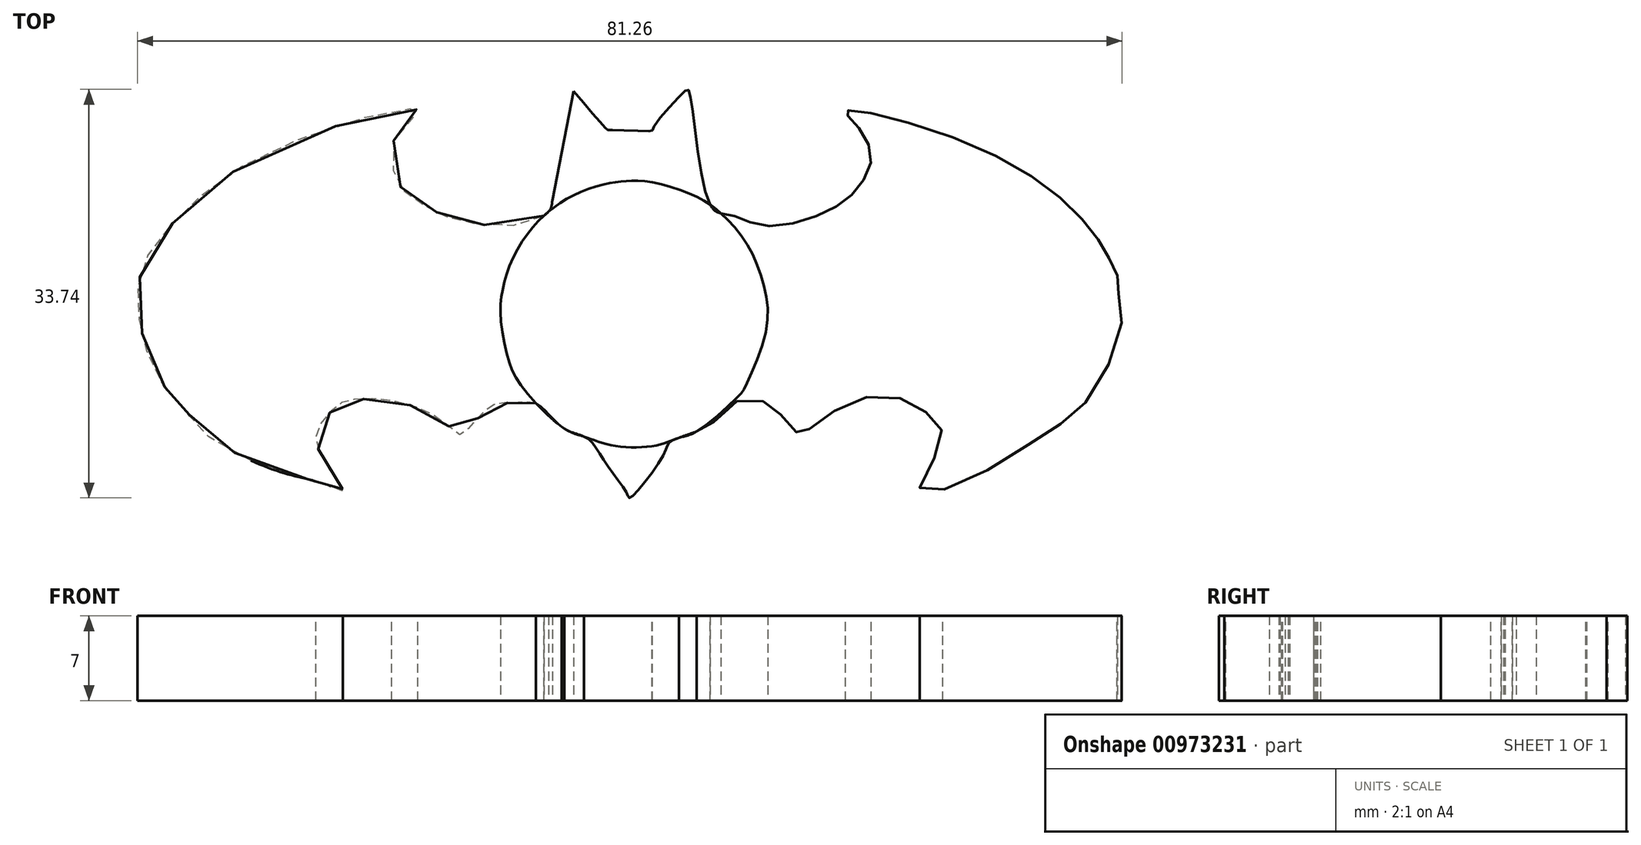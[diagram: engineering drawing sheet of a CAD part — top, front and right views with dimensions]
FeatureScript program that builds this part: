
annotation { "Feature Type Name" : "Feature", "Feature Type Description" : "" }
export const myFeature = defineFeature(function(context is Context, id is Id, definition is map)
    precondition{}
    {
        {
            var Q0;
            Q0=qCreatedBy(makeId("Top.planeOp"),FACE);
            var sketch = newSketch(context, id + "F0", { "sketchPlane" : qUnion([Q0])});
            skFitSpline(sketch, "E0", {"points": [v(-4.97, 18.4) * mm, v(-2.22, 15.26) * mm, v(-2.02, 15.22) * mm, v(1.53, 15.14) * mm, v(1.53, 15.22) * mm, v(4.16, 18.37) * mm, v(4.56, 18.45) * mm, v(6.34, 8.99) * mm, v(7.99, 8.2) * mm, v(10.58, 7.33) * mm, v(15.52, 8.29) * mm, v(18.5, 10.4) * mm, v(19.58, 13.3) * mm, v(17.99, 16.06) * mm, v(17.51, 16.78) * mm, v(28.87, 13.55) * mm, v(37.9, 6.79) * mm, v(39.94, 3.16) * mm], "startDerivative": vector(56.58, -66.21) * mm, "endDerivative": vector(23.78, -52.66) * mm});
            skFitSpline(sketch, "E1", {"points": [v(39.94, 3.16) * mm, v(39.94, 2.1) * mm, v(40.27, -0.8) * mm, v(37.31, -7.26) * mm, v(34.01, -9.85) * mm, v(27.07, -13.94) * mm, v(23.62, -14.4) * mm, v(25.45, -10.55) * mm, v(24.94, -8.9) * mm, v(22.76, -7.23) * mm, v(18.8, -6.97) * mm, v(15.07, -9.06) * mm, v(13.72, -9.9) * mm, v(13.34, -9.66) * mm, v(11.82, -7.96) * mm, v(10.39, -7.15) * mm, v(8.28, -7.24) * mm, v(8.2, -7.33) * mm, v(7.45, -8.22) * mm, v(6.45, -9.02) * mm, v(5.19, -9.7) * mm, v(2.95, -10.6) * mm, v(2.55, -11.48) * mm, v(-0.32, -15.17) * mm, v(-0.52, -14.9) * mm, v(-2.3, -12.33) * mm, v(-3.7, -10.36) * mm, v(-4.97, -9.81) * mm, v(-6.29, -9.03) * mm, v(-8.25, -7.28) * mm, v(-9.37, -7.31) * mm, v(-10.15, -7.31) * mm, v(-11.2, -7.4) * mm, v(-11.98, -7.71) * mm, v(-14.2, -9.96) * mm, v(-14.44, -9.9) * mm, v(-16.48, -8.38) * mm, v(-18.28, -7.59) * mm, v(-20.56, -7.06) * mm, v(-23.45, -7.11) * mm, v(-24.54, -7.6) * mm, v(-26.03, -9.39) * mm, v(-26.08, -11.07) * mm, v(-24.47, -13.8) * mm, v(-24.04, -14.6) * mm, v(-25.18, -14.15) * mm, v(-30.01, -12.75) * mm, v(-36.3, -9.08) * mm, v(-36.84, -7.97) * mm, v(-37.85, -7.07) * mm, v(-39.83, -3.97) * mm, v(-40.86, 0) * mm, v(-40.57, 3.8) * mm, v(-37.46, 8.14) * mm, v(-29.77, 13.55) * mm, v(-18.12, 16.95) * mm, v(-17.85, 16.66) * mm, v(-19.52, 14.96) * mm, v(-19.8, 11.64) * mm, v(-18.75, 10) * mm, v(-16.57, 8.59) * mm, v(-14.93, 7.88) * mm, v(-10.07, 7.33) * mm, v(-7.02, 8.47) * mm, v(-6.72, 9.4) * mm], "startDerivative": vector(-9.1, -93.87) * mm, "endDerivative": vector(8.09, 94.73) * mm});
            skFitSpline(sketch, "E2", {"points": [v(-6.72, 9.4) * mm, v(-4.97, 18.4) * mm], "startDerivative": vector(1.75, 9.02) * mm, "endDerivative": vector(1.75, 9.02) * mm});
            skFitSpline(sketch, "E3", {"points": [v(7.24, 8.29) * mm, v(9.3, 5.88) * mm, v(10.72, 2.48) * mm, v(10.9, -1.49) * mm, v(9.2, -6.04) * mm, v(8.72, -6.71) * mm, v(5.19, -9.7) * mm, v(3.73, -10.22) * mm, v(2.16, -10.79) * mm, v(-1.65, -10.87) * mm, v(-4.1, -10.12) * mm, v(-5.72, -9.47) * mm, v(-9.2, -6.02) * mm, v(-10.36, -3.69) * mm, v(-11, 0) * mm, v(-10.8, 2.05) * mm, v(-10.12, 4.32) * mm, v(-8.64, 6.81) * mm, v(-7.02, 8.47) * mm, v(-4.78, 9.9) * mm, v(-2.14, 10.8) * mm, v(-0.65, 10.98) * mm, v(1.26, 10.93) * mm, v(5.19, 9.7) * mm, v(7.24, 8.29) * mm]});
            skSolve(sketch);
        }
        {
            var Q0;
            {var subQ0=sQuery(id+"F0.wireOp",EDGE,"E2");Q0=makeQuery(id+"F0.imprint","IMPRINT",FACE,{"disambiguationData":[TD([[makeQuery(id+"F0.imprint","IMPRINT",EDGE,{"derivedFrom":subQ0}),-1.0]])]});}
            var Q1;
            {var subQ0=sQuery(id+"F0.wireOp",EDGE,"E3");var subQ1=sQuery(id+"F0.wireOp",EDGE,"E0");var subQ2=makeQuery(id+"F0.imprint","INTERSECT",VERTEX,{"disambiguationData":[OD(0.0)],"derivedFrom":[subQ1,subQ0]});Q1=makeQuery(id+"F0.imprint","IMPRINT",FACE,{"disambiguationData":[TD([[makeQuery(id+"F0.imprint","IMPRINT",EDGE,{"disambiguationData":[TD([[subQ2,-1.0]])],"derivedFrom":subQ1}),1.0]])]});}
            var Q2;
            {var subQ0=sQuery(id+"F0.wireOp",EDGE,"E1");var subQ1=sQuery(id+"F0.wireOp",EDGE,"E0");var subQ2=makeQuery(id+"F0.imprint","INTERSECT",VERTEX,{"derivedFrom":[subQ1,subQ0]});Q2=makeQuery(id+"F0.imprint","IMPRINT",FACE,{"disambiguationData":[TD([[makeQuery(id+"F0.imprint","IMPRINT",EDGE,{"disambiguationData":[TD([[subQ2,1.0]])],"derivedFrom":subQ1}),-1.0]])]});}
            var Q3;
            {var subQ0=sQuery(id+"F0.wireOp",EDGE,"E3");var subQ1=sQuery(id+"F0.wireOp",EDGE,"E1");var subQ2=makeQuery(id+"F0.imprint","INTERSECT",VERTEX,{"disambiguationData":[OD(0.0)],"derivedFrom":[subQ1,subQ0]});Q3=makeQuery(id+"F0.imprint","IMPRINT",FACE,{"disambiguationData":[TD([[makeQuery(id+"F0.imprint","IMPRINT",EDGE,{"disambiguationData":[TD([[subQ2,-1.0]])],"derivedFrom":subQ1}),1.0]])]});}
            var Q4;
            {var subQ0=sQuery(id+"F0.wireOp",EDGE,"E3");var subQ1=sQuery(id+"F0.wireOp",EDGE,"E1");var subQ2=makeQuery(id+"F0.imprint","INTERSECT",VERTEX,{"disambiguationData":[OD(1.0)],"derivedFrom":[subQ1,subQ0]});Q4=makeQuery(id+"F0.imprint","IMPRINT",FACE,{"disambiguationData":[TD([[makeQuery(id+"F0.imprint","IMPRINT",EDGE,{"disambiguationData":[TD([[subQ2,-1.0]])],"derivedFrom":subQ1}),-1.0]])]});}
            var Q5;
            {var subQ0=sQuery(id+"F0.wireOp",EDGE,"E3");var subQ1=sQuery(id+"F0.wireOp",EDGE,"E1");var subQ2=makeQuery(id+"F0.imprint","INTERSECT",VERTEX,{"disambiguationData":[OD(2.0)],"derivedFrom":[subQ1,subQ0]});Q5=makeQuery(id+"F0.imprint","IMPRINT",FACE,{"disambiguationData":[TD([[makeQuery(id+"F0.imprint","IMPRINT",EDGE,{"disambiguationData":[TD([[subQ2,-1.0]])],"derivedFrom":subQ1}),1.0]])]});}
            var Q6;
            {var subQ0=sQuery(id+"F0.wireOp",EDGE,"E3");var subQ1=sQuery(id+"F0.wireOp",EDGE,"E1");var subQ2=makeQuery(id+"F0.imprint","INTERSECT",VERTEX,{"disambiguationData":[OD(3.0)],"derivedFrom":[subQ1,subQ0]});Q6=makeQuery(id+"F0.imprint","IMPRINT",FACE,{"disambiguationData":[TD([[makeQuery(id+"F0.imprint","IMPRINT",EDGE,{"disambiguationData":[TD([[subQ2,-1.0]])],"derivedFrom":subQ1}),-1.0]])]});}
            var Q7;
            {var subQ0=sQuery(id+"F0.wireOp",EDGE,"E3");var subQ1=sQuery(id+"F0.wireOp",EDGE,"E1");var subQ2=makeQuery(id+"F0.imprint","INTERSECT",VERTEX,{"disambiguationData":[OD(4.0)],"derivedFrom":[subQ1,subQ0]});Q7=makeQuery(id+"F0.imprint","IMPRINT",FACE,{"disambiguationData":[TD([[makeQuery(id+"F0.imprint","IMPRINT",EDGE,{"disambiguationData":[TD([[subQ2,-1.0]])],"derivedFrom":subQ1}),1.0]])]});}
            var Q8;
            {var subQ0=sQuery(id+"F0.wireOp",EDGE,"E3");var subQ1=sQuery(id+"F0.wireOp",EDGE,"E1");var subQ2=makeQuery(id+"F0.imprint","INTERSECT",VERTEX,{"disambiguationData":[OD(5.0)],"derivedFrom":[subQ1,subQ0]});Q8=makeQuery(id+"F0.imprint","IMPRINT",FACE,{"disambiguationData":[TD([[makeQuery(id+"F0.imprint","IMPRINT",EDGE,{"disambiguationData":[TD([[subQ2,-1.0]])],"derivedFrom":subQ1}),-1.0]])]});}
            var Q9;
            {var subQ0=sQuery(id+"F0.wireOp",EDGE,"E3");var subQ1=sQuery(id+"F0.wireOp",EDGE,"E1");var subQ2=makeQuery(id+"F0.imprint","INTERSECT",VERTEX,{"disambiguationData":[OD(6.0)],"derivedFrom":[subQ1,subQ0]});Q9=makeQuery(id+"F0.imprint","IMPRINT",FACE,{"disambiguationData":[TD([[makeQuery(id+"F0.imprint","IMPRINT",EDGE,{"disambiguationData":[TD([[subQ2,-1.0]])],"derivedFrom":subQ1}),1.0]])]});}
            extrude(context, id + "F1", {"entities" : qUnion([Q0, Q1, Q2, Q3, Q4, Q5, Q6, Q7, Q8, Q9]), "depth" : 7 * mm, "offsetDistance" : 25.4 * mm});
        }
    });
